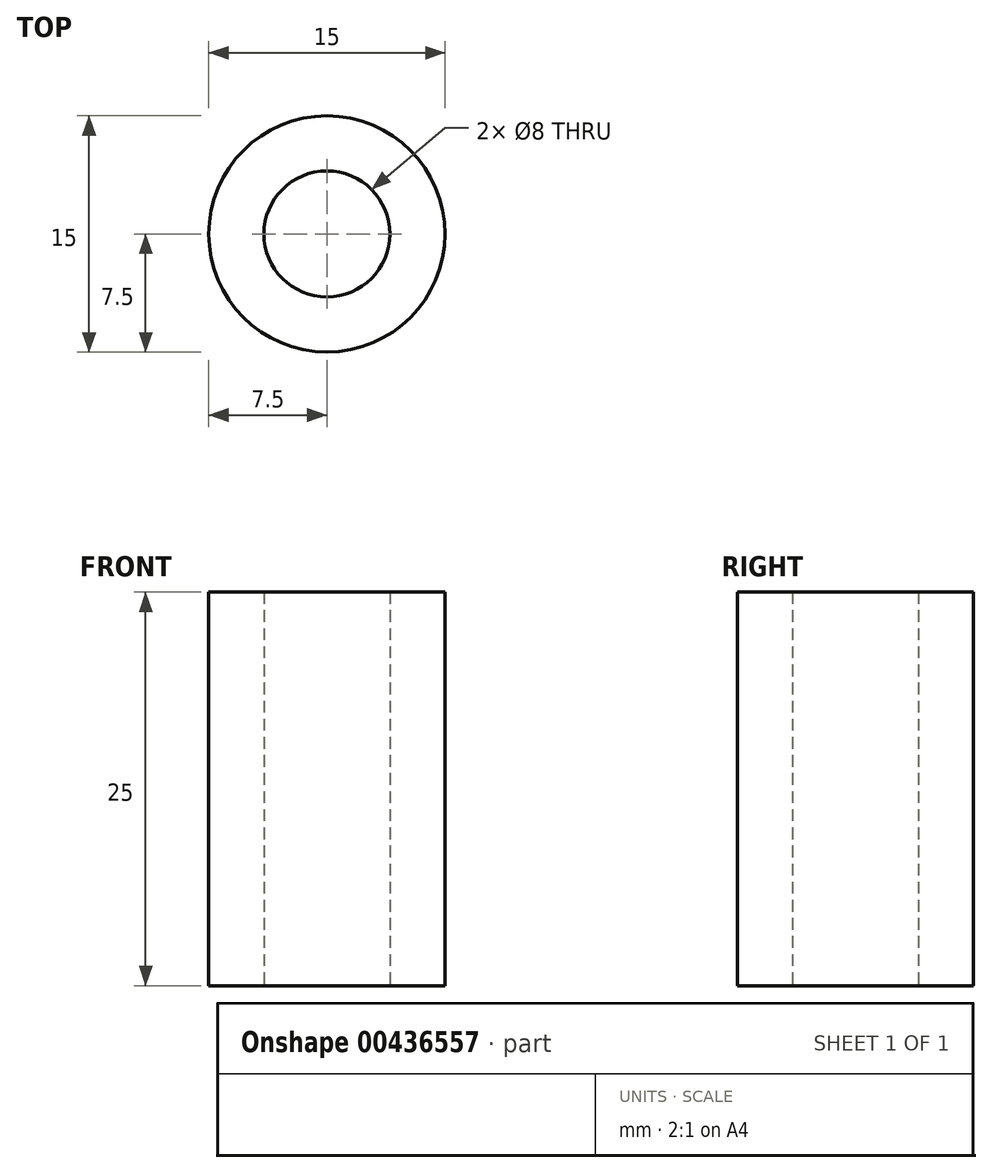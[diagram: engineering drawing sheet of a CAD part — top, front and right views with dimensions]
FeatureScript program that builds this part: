
annotation { "Feature Type Name" : "Feature", "Feature Type Description" : "" }
export const myFeature = defineFeature(function(context is Context, id is Id, definition is map)
    precondition{}
    {
        {
            var Q0;
            Q0=qCreatedBy(makeId("Top.planeOp"),FACE);
            var sketch = newSketch(context, id + "F0", { "sketchPlane" : qUnion([Q0])});
            skCircle(sketch, "E0", {"center": v(0, 0) * mm, "radius": 7.5 * mm});
            skCircle(sketch, "E1", {"center": v(0, 0) * mm, "radius": 4 * mm});
            skSolve(sketch);
        }
        {
            var Q0;
            Q0=makeQuery(id+"F0.imprint","IMPRINT",FACE,{"disambiguationData":[TD([[makeQuery(id+"F0.imprint","IMPRINT",EDGE,{"derivedFrom":sQuery(id+"F0.wireOp",EDGE,"E0")}),1.0]])]});
            extrude(context, id + "F1", {"entities" : qUnion([Q0]), "depth" : 25 * mm});
        }
    });
